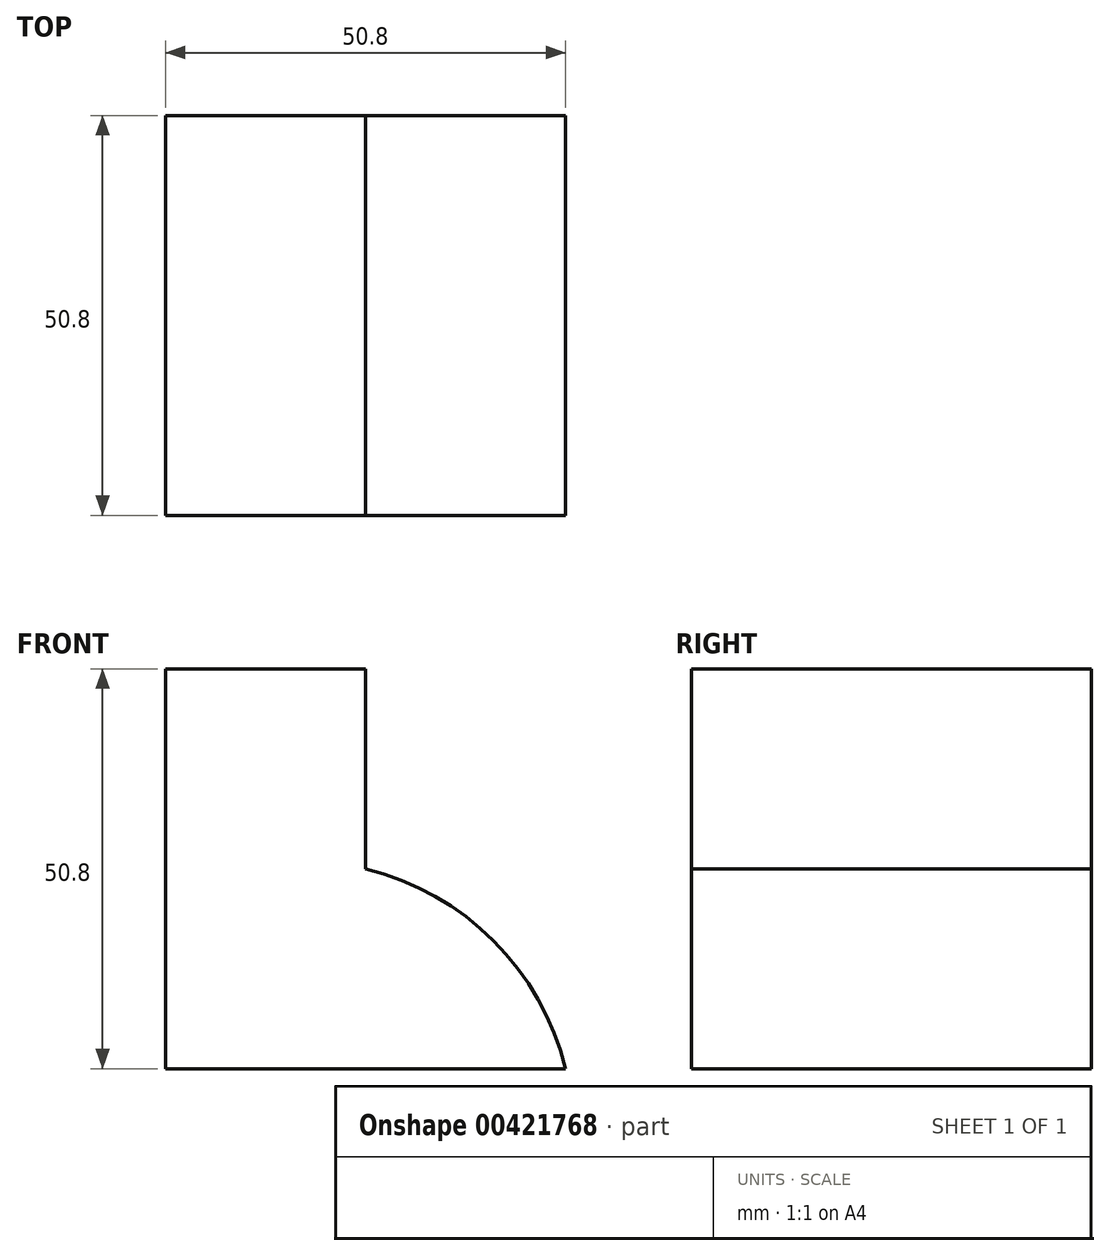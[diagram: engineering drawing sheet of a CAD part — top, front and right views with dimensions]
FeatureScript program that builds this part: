
annotation { "Feature Type Name" : "Feature", "Feature Type Description" : "" }
export const myFeature = defineFeature(function(context is Context, id is Id, definition is map)
    precondition{}
    {
        {
            var Q0;
            Q0=qCreatedBy(makeId("Front.planeOp"),FACE);
            var sketch = newSketch(context, id + "F0", { "sketchPlane" : qUnion([Q0])});
            skLineSegment(sketch, "E0", {"start": v(0, 0) * mm, "end": v(0, 50.8) * mm});
            skLineSegment(sketch, "E1", {"start": v(0, 50.8) * mm, "end": v(25.4, 50.8) * mm});
            skLineSegment(sketch, "E2", {"start": v(25.4, 50.8) * mm, "end": v(25.4, 25.4) * mm});
            skLineSegment(sketch, "E3", {"start": v(0, 0) * mm, "end": v(50.8, 0) * mm});
            skArc(sketch, "E4", {"start": v(50.8, 0) * mm, "mid": v(41.65, 16.25) * mm, "end": v(25.4, 25.4) * mm});
            skSolve(sketch);
        }
        {
            var Q0;
            Q0 = qSketchRegion(id + "F0", true);
            extrude(context, id + "F1", {"entities" : qUnion([Q0]), "depth" : 50.8 * mm});
        }
    });
